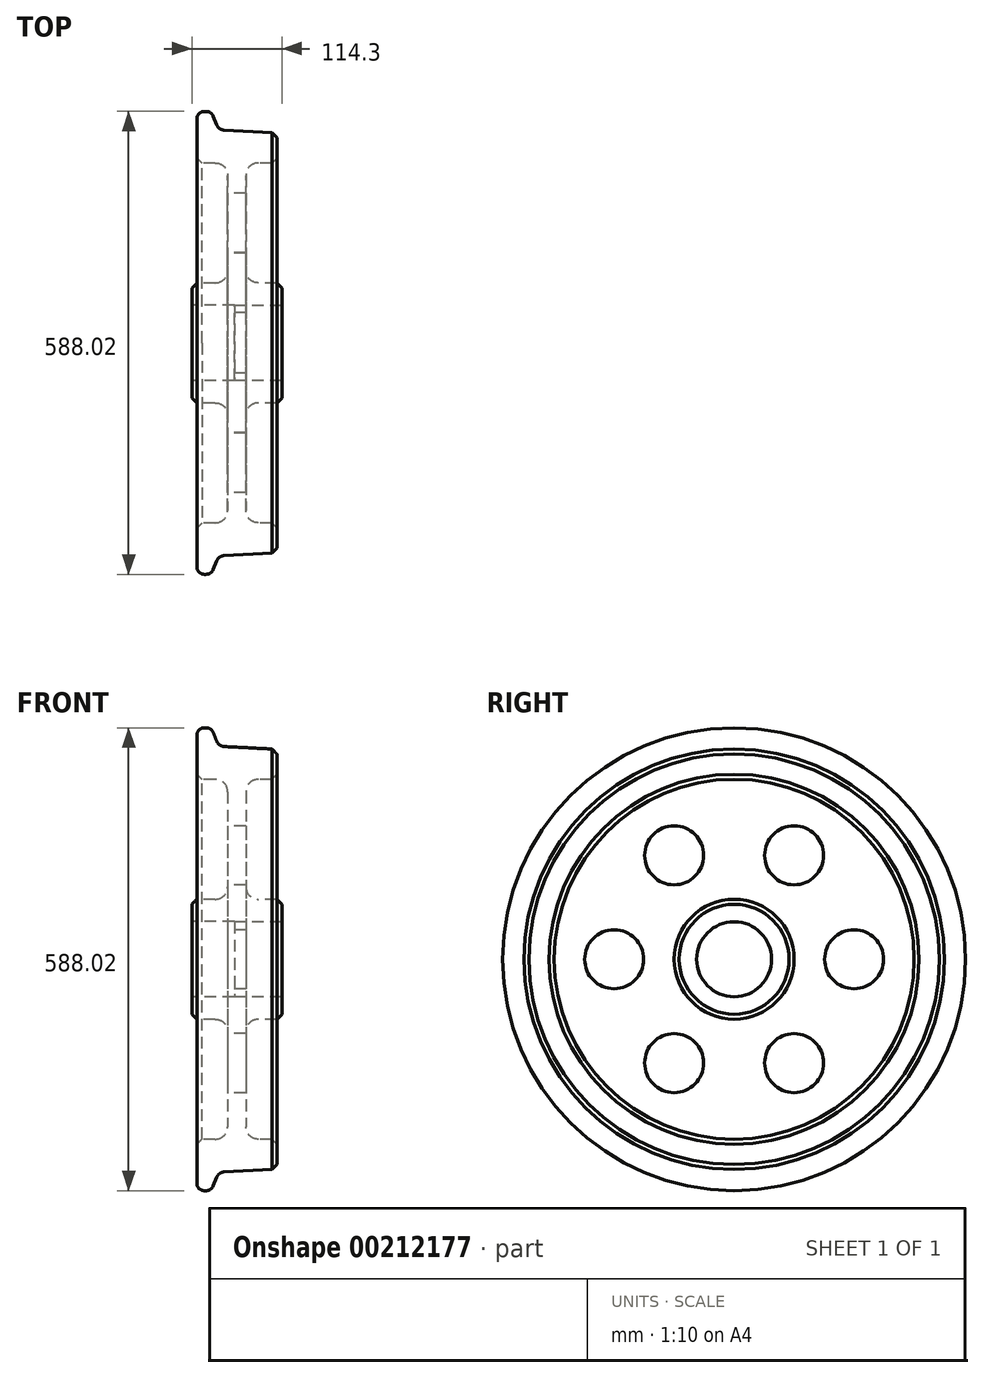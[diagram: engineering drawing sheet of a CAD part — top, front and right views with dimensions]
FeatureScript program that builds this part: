
annotation { "Feature Type Name" : "Feature", "Feature Type Description" : "" }
export const myFeature = defineFeature(function(context is Context, id is Id, definition is map)
    precondition{}
    {
        {
            var Q0;
            Q0=qCreatedBy(makeId("Top.planeOp"),FACE);
            var sketch = newSketch(context, id + "F0", { "sketchPlane" : qUnion([Q0])});
            skLineSegment(sketch, "E0", {"start": v(0, 0) * mm, "end": v(0, 294) * mm, "construction": true});
            skLineSegment(sketch, "E1.0", {"start": v(114.3, 0) * mm, "end": v(114.3, 294) * mm, "construction": true});
            skLineSegment(sketch, "E2.0", {"start": v(57.15, 0) * mm, "end": v(57.15, 294) * mm, "construction": true});
            skLineSegment(sketch, "E3", {"start": v(0, 0) * mm, "end": v(114.3, 0) * mm, "construction": true});
            skLineSegment(sketch, "E4", {"start": v(0, 0) * mm, "end": v(0, 76.2) * mm});
            skLineSegment(sketch, "E5", {"start": v(0, 76.2) * mm, "end": v(29.78, 76.2) * mm});
            skLineSegment(sketch, "E6", {"start": v(45.65, 92.08) * mm, "end": v(45.65, 212.72) * mm});
            skLineSegment(sketch, "E7", {"start": v(45.65, 76.2) * mm, "end": v(57.15, 76.2) * mm, "construction": true});
            skLineSegment(sketch, "E8", {"start": v(57.15, 76.2) * mm, "end": v(68.65, 76.2) * mm, "construction": true});
            skPoint(sketch, "E9.visualSharp", {"position": v(45.65, 76.2) * mm});
            skArc(sketch, "E9.filletArc", {"start": v(29.78, 76.2) * mm, "mid": v(41, 80.85) * mm, "end": v(45.65, 92.08) * mm});
            skLineSegment(sketch, "E10.MirrorCS", {"start": v(114.3, 0) * mm, "end": v(114.3, 76.2) * mm});
            skLineSegment(sketch, "E11.MirrorCS", {"start": v(68.65, 92.08) * mm, "end": v(68.65, 212.72) * mm});
            skLineSegment(sketch, "E12.MirrorCS", {"start": v(114.3, 76.2) * mm, "end": v(84.53, 76.2) * mm});
            skArc(sketch, "E13.MirrorCS", {"start": v(84.53, 76.2) * mm, "mid": v(73.3, 80.85) * mm, "end": v(68.65, 92.08) * mm});
            skLineSegment(sketch, "E14", {"start": v(114.3, 47.63) * mm, "end": v(138.85, 47.63) * mm, "construction": true});
            skLineSegment(sketch, "E15", {"start": v(0, 47.7) * mm, "end": v(-14.3, 47.7) * mm, "construction": true});
            skLineSegment(sketch, "E16", {"start": v(54, 67.26) * mm, "end": v(54, -20.55) * mm, "construction": true});
            skLineSegment(sketch, "E17", {"start": v(0, 47.7) * mm, "end": v(54, 47.7) * mm});
            skLineSegment(sketch, "E18", {"start": v(114.3, 47.63) * mm, "end": v(54, 47.63) * mm});
            skLineSegment(sketch, "E19", {"start": v(54, 47.7) * mm, "end": v(54, 47.63) * mm});
            skLineSegment(sketch, "E20", {"start": v(0, 294) * mm, "end": v(6.35, 294) * mm, "construction": true});
            skLineSegment(sketch, "E21", {"start": v(6.35, 284.5) * mm, "end": v(6.35, 228.6) * mm});
            skLineSegment(sketch, "E22", {"start": v(6.35, 228.6) * mm, "end": v(29.78, 228.6) * mm});
            skLineSegment(sketch, "E23", {"start": v(15.85, 294) * mm, "end": v(15.85, 301.95) * mm, "construction": true});
            skLineSegment(sketch, "E24.0", {"start": v(18.35, 294) * mm, "end": v(18.35, 301.95) * mm, "construction": true});
            skLineSegment(sketch, "E25", {"start": v(15.85, 294) * mm, "end": v(18.35, 294) * mm});
            skLineSegment(sketch, "E26", {"start": v(15.85, 294) * mm, "end": v(15.85, 294) * mm});
            skPoint(sketch, "E27.visualSharp", {"position": v(6.35, 294) * mm});
            skArc(sketch, "E27.filletArc", {"start": v(15.85, 294) * mm, "mid": v(9.13, 291.22) * mm, "end": v(6.35, 284.5) * mm});
            skLineSegment(sketch, "E28", {"start": v(114.3, 294) * mm, "end": v(107.95, 294) * mm, "construction": true});
            skLineSegment(sketch, "E29", {"start": v(107.95, 294) * mm, "end": v(107.95, 266.7) * mm, "construction": true});
            skLineSegment(sketch, "E30", {"start": v(84.53, 228.6) * mm, "end": v(107.95, 228.6) * mm});
            skLineSegment(sketch, "E31", {"start": v(107.95, 228.6) * mm, "end": v(107.95, 266.7) * mm});
            skLineSegment(sketch, "E32", {"start": v(107.95, 266.7) * mm, "end": v(41.23, 270.2) * mm});
            skLineSegment(sketch, "E33", {"start": v(18.35, 294) * mm, "end": v(18.35, 284.5) * mm, "construction": true});
            skArc(sketch, "E34", {"start": v(18.35, 294) * mm, "mid": v(23.66, 292.38) * mm, "end": v(27.16, 288.06) * mm});
            skLineSegment(sketch, "E35", {"start": v(27.16, 288.06) * mm, "end": v(31.6, 277.06) * mm});
            skPoint(sketch, "E36.orphan", {"position": v(18.35, 275) * mm});
            skPoint(sketch, "E37.visualSharp", {"position": v(34.23, 270.56) * mm});
            skArc(sketch, "E37.filletArc", {"start": v(31.6, 277.06) * mm, "mid": v(35.41, 272.23) * mm, "end": v(41.23, 270.2) * mm});
            skPoint(sketch, "E38.visualSharp", {"position": v(68.65, 228.6) * mm});
            skArc(sketch, "E38.filletArc", {"start": v(84.53, 228.6) * mm, "mid": v(73.3, 223.95) * mm, "end": v(68.65, 212.73) * mm});
            skPoint(sketch, "E39.visualSharp", {"position": v(45.65, 228.6) * mm});
            skArc(sketch, "E39.filletArc", {"start": v(45.65, 212.72) * mm, "mid": v(41, 223.95) * mm, "end": v(29.78, 228.6) * mm});
            skSolve(sketch);
        }
        {
            var Q0;
            {var subQ2=sQuery(id+"F0.wireOp",EDGE,"E5");Q0=makeQuery(id+"F0.imprint","IMPRINT",FACE,{"disambiguationData":[TD([[makeQuery(id+"F0.imprint","IMPRINT",EDGE,{"derivedFrom":subQ2}),-1.0]])]});}
            var Q1;
            Q1=sQuery(id+"F0.wireOp",EDGE,"E3");
            revolve(context, id + "F1", {"entities" : qUnion([Q0]), "axis" : qUnion([Q1]), "revolveType" : RevolveType.FULL});
        }
        {
            var Q0;
            Q0=makeQuery(id+"F1.opRevolve","SWEPT_EDGE",EDGE,{"disambiguationData":[OSD([sQuery(id+"F0.wireOp",EDGE,"E31"),sQuery(id+"F0.wireOp",EDGE,"E32")])]});
            var Q1;
            Q1=makeQuery(id+"F1.opRevolve","SWEPT_EDGE",EDGE,{"disambiguationData":[OSD([sQuery(id+"F0.wireOp",EDGE,"E30"),sQuery(id+"F0.wireOp",EDGE,"E31")])]});
            var Q2;
            Q2=makeQuery(id+"F1.opRevolve","SWEPT_EDGE",EDGE,{"disambiguationData":[OSD([sQuery(id+"F0.wireOp",EDGE,"E10.MirrorCS"),sQuery(id+"F0.wireOp",EDGE,"E12.MirrorCS")])]});
            var Q3;
            Q3=makeQuery(id+"F1.opRevolve","SWEPT_EDGE",EDGE,{"disambiguationData":[OSD([sQuery(id+"F0.wireOp",EDGE,"E4"),sQuery(id+"F0.wireOp",EDGE,"E5")])]});
            var Q4;
            Q4=makeQuery(id+"F1.opRevolve","SWEPT_EDGE",EDGE,{"disambiguationData":[OSD([sQuery(id+"F0.wireOp",EDGE,"E21"),sQuery(id+"F0.wireOp",EDGE,"E22")])]});
            chamfer(context, id + "F2", {"entities" : qUnion([Q0, Q1, Q2, Q3, Q4]), "width" : 6.35 * mm, "tangentPropagation" : true});
        }
        {
            var Q0;
            Q0=qCreatedBy(makeId("Right.planeOp"),FACE);
            var sketch = newSketch(context, id + "F3", { "sketchPlane" : qUnion([Q0])});
            skLineSegment(sketch, "E40", {"start": v(0, 0) * mm, "end": v(-152.4, 0) * mm, "construction": true});
            skLineSegment(sketch, "E41", {"start": v(0, 0) * mm, "end": v(152.4, 0) * mm, "construction": true});
            skCircle(sketch, "E42", {"center": v(-152.4, 0) * mm, "radius": 37.5 * mm});
            skCircle(sketch, "E43.1.0", {"center": v(-76.2, -131.98) * mm, "radius": 37.5 * mm});
            skCircle(sketch, "E43.2.0", {"center": v(76.2, -131.98) * mm, "radius": 37.5 * mm});
            skCircle(sketch, "E43.3.0", {"center": v(152.4, 0) * mm, "radius": 37.5 * mm});
            skCircle(sketch, "E43.4.0", {"center": v(76.2, 131.98) * mm, "radius": 37.5 * mm});
            skCircle(sketch, "E43.5.0", {"center": v(-76.2, 131.98) * mm, "radius": 37.5 * mm});
            skPoint(sketch, "E43.center", {"position": v(0, 0) * mm});
            skSolve(sketch);
        }
        {
            var Q0;
            Q0=makeQuery(id+"F3.imprint","IMPRINT",FACE,{"disambiguationData":[TD([[makeQuery(id+"F3.imprint","IMPRINT",EDGE,{"derivedFrom":sQuery(id+"F3.wireOp",EDGE,"E42")}),1.0]])]});
            var Q1;
            Q1=makeQuery(id+"F3.imprint","IMPRINT",FACE,{"disambiguationData":[TD([[makeQuery(id+"F3.imprint","IMPRINT",EDGE,{"derivedFrom":sQuery(id+"F3.wireOp",EDGE,"E43.5.0")}),1.0]])]});
            var Q2;
            Q2=makeQuery(id+"F3.imprint","IMPRINT",FACE,{"disambiguationData":[TD([[makeQuery(id+"F3.imprint","IMPRINT",EDGE,{"derivedFrom":sQuery(id+"F3.wireOp",EDGE,"E43.4.0")}),1.0]])]});
            var Q3;
            Q3=makeQuery(id+"F3.imprint","IMPRINT",FACE,{"disambiguationData":[TD([[makeQuery(id+"F3.imprint","IMPRINT",EDGE,{"derivedFrom":sQuery(id+"F3.wireOp",EDGE,"E43.3.0")}),1.0]])]});
            var Q4;
            Q4=makeQuery(id+"F3.imprint","IMPRINT",FACE,{"disambiguationData":[TD([[makeQuery(id+"F3.imprint","IMPRINT",EDGE,{"derivedFrom":sQuery(id+"F3.wireOp",EDGE,"E43.2.0")}),1.0]])]});
            var Q5;
            Q5=makeQuery(id+"F3.imprint","IMPRINT",FACE,{"disambiguationData":[TD([[makeQuery(id+"F3.imprint","IMPRINT",EDGE,{"derivedFrom":sQuery(id+"F3.wireOp",EDGE,"E43.1.0")}),1.0]])]});
            extrude(context, id + "F4", {"entities" : qUnion([Q0, Q1, Q2, Q3, Q4, Q5]), "operationType" : NewBodyOperationType.REMOVE, "endBound" : BoundingType.THROUGH_ALL, "depth" : 25.4 * mm});
        }
    });
